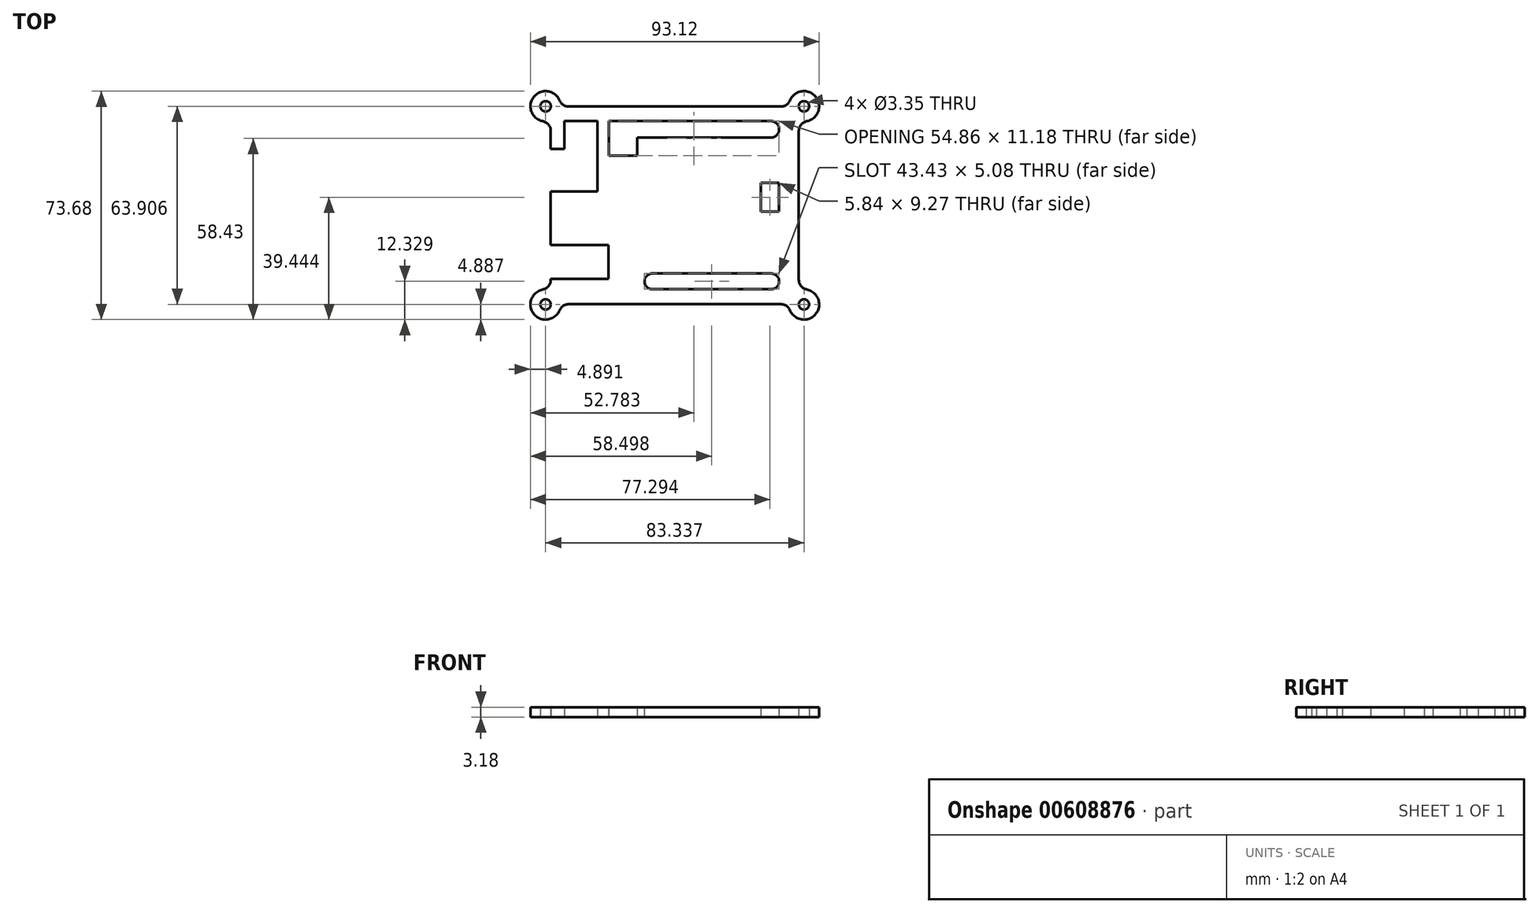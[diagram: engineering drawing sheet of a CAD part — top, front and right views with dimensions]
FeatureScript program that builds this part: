
annotation { "Feature Type Name" : "Feature", "Feature Type Description" : "" }
export const myFeature = defineFeature(function(context is Context, id is Id, definition is map)
    precondition{}
    {
        {
            var Q0;
            Q0=qCreatedBy(makeId("Top.planeOp"),FACE);
            var sketch = newSketch(context, id + "F0", { "sketchPlane" : qUnion([Q0])});
            skPoint(sketch, "E0.middle", {"position": v(0, 0) * mm});
            skLineSegment(sketch, "E1.bottom", {"start": v(-34.22, 31.88) * mm, "end": v(34.22, 31.88) * mm});
            skLineSegment(sketch, "E1.top", {"start": v(-34.22, -31.88) * mm, "end": v(34.22, -31.88) * mm});
            skLineSegment(sketch, "E1.left", {"start": v(-40, 24.03) * mm, "end": v(-40, 18.16) * mm});
            skLineSegment(sketch, "E1.right", {"start": v(40, 24.03) * mm, "end": v(40, -24.03) * mm});
            skArc(sketch, "E2", {"start": v(-37.15, 33.83) * mm, "mid": v(-45.46, 35.04) * mm, "end": v(-42.58, 27.15) * mm});
            skArc(sketch, "E3.filletArc", {"start": v(-37.15, 33.83) * mm, "mid": v(-35.98, 32.41) * mm, "end": v(-34.22, 31.88) * mm});
            skArc(sketch, "E4.filletArc", {"start": v(-40, 24.03) * mm, "mid": v(-40.73, 26.06) * mm, "end": v(-42.58, 27.15) * mm});
            skArc(sketch, "E5", {"start": v(-42.59, -27.15) * mm, "mid": v(-45.46, -35.04) * mm, "end": v(-37.15, -33.83) * mm});
            skArc(sketch, "E6.filletArc", {"start": v(-42.59, -27.15) * mm, "mid": v(-40.73, -26.06) * mm, "end": v(-40, -24.03) * mm});
            skArc(sketch, "E7.filletArc", {"start": v(-34.22, -31.88) * mm, "mid": v(-35.99, -32.41) * mm, "end": v(-37.15, -33.83) * mm});
            skArc(sketch, "E8", {"start": v(37.15, -33.83) * mm, "mid": v(45.46, -35.04) * mm, "end": v(42.59, -27.15) * mm});
            skArc(sketch, "E9.filletArc", {"start": v(40, -24.03) * mm, "mid": v(40.73, -26.06) * mm, "end": v(42.59, -27.15) * mm});
            skArc(sketch, "E10.filletArc", {"start": v(37.15, -33.83) * mm, "mid": v(35.99, -32.41) * mm, "end": v(34.22, -31.88) * mm});
            skArc(sketch, "E11", {"start": v(42.59, 27.15) * mm, "mid": v(45.46, 35.04) * mm, "end": v(37.15, 33.83) * mm});
            skArc(sketch, "E12.filletArc", {"start": v(34.22, 31.88) * mm, "mid": v(35.99, 32.41) * mm, "end": v(37.15, 33.83) * mm});
            skArc(sketch, "E13.filletArc", {"start": v(42.59, 27.15) * mm, "mid": v(40.73, 26.06) * mm, "end": v(40, 24.03) * mm});
            skCircle(sketch, "E14", {"center": v(-41.66, 31.95) * mm, "radius": 1.68 * mm});
            skCircle(sketch, "E15", {"center": v(-41.67, -31.95) * mm, "radius": 1.68 * mm});
            skCircle(sketch, "E16", {"center": v(41.67, -31.95) * mm, "radius": 1.68 * mm});
            skCircle(sketch, "E17", {"center": v(41.67, 31.95) * mm, "radius": 1.68 * mm});
            skLineSegment(sketch, "E18.0", {"start": v(-35.56, 27.18) * mm, "end": v(-24.9, 27.18) * mm});
            skLineSegment(sketch, "E19.0", {"start": v(-35.56, 27.18) * mm, "end": v(-35.56, 18.16) * mm});
            skLineSegment(sketch, "E20.0", {"start": v(-24.9, 27.18) * mm, "end": v(-24.9, 4.45) * mm});
            skLineSegment(sketch, "E21.0", {"start": v(-35.56, 4.45) * mm, "end": v(-24.9, 4.45) * mm});
            skLineSegment(sketch, "E22", {"start": v(-35.56, 18.16) * mm, "end": v(-40, 18.16) * mm});
            skLineSegment(sketch, "E23", {"start": v(-35.56, 4.45) * mm, "end": v(-40, 4.45) * mm});
            skLineSegment(sketch, "E24.trimOffspring", {"start": v(-40, 4.45) * mm, "end": v(-40, -12.83) * mm});
            skLineSegment(sketch, "E25.0", {"start": v(-40, -12.83) * mm, "end": v(-21.34, -12.83) * mm});
            skLineSegment(sketch, "E26.0", {"start": v(-40, -23.75) * mm, "end": v(-21.34, -23.75) * mm});
            skLineSegment(sketch, "E27.0", {"start": v(-21.34, -12.83) * mm, "end": v(-21.34, -23.75) * mm});
            skLineSegment(sketch, "E28.trimOffspring", {"start": v(-40, -23.75) * mm, "end": v(-40, -24.03) * mm});
            skLineSegment(sketch, "E29.0", {"start": v(-21.2, 27.18) * mm, "end": v(-21.2, 16) * mm});
            skLineSegment(sketch, "E30.trimOffspring", {"start": v(-12.07, 21.84) * mm, "end": v(30.99, 21.84) * mm});
            skLineSegment(sketch, "E31.trimOffspring", {"start": v(-21.2, 27.18) * mm, "end": v(30.99, 27.18) * mm});
            skLineSegment(sketch, "E32.0", {"start": v(-21.2, 16) * mm, "end": v(-12.07, 16) * mm});
            skLineSegment(sketch, "E33", {"start": v(-12.07, 21.84) * mm, "end": v(-12.07, 16) * mm});
            skLineSegment(sketch, "E34.0", {"start": v(33.65, 24.51) * mm, "end": v(33.65, 24.51) * mm});
            skArc(sketch, "E35.filletArc", {"start": v(33.65, 24.51) * mm, "mid": v(32.87, 26.4) * mm, "end": v(30.99, 27.18) * mm});
            skArc(sketch, "E36.filletArc", {"start": v(30.99, 21.84) * mm, "mid": v(32.87, 22.63) * mm, "end": v(33.65, 24.51) * mm});
            skLineSegment(sketch, "E37.0", {"start": v(-7.24, -27.05) * mm, "end": v(31.12, -27.05) * mm});
            skLineSegment(sketch, "E38.0", {"start": v(33.66, -24.51) * mm, "end": v(33.66, -24.51) * mm});
            skLineSegment(sketch, "E39.0", {"start": v(-9.78, 24.03) * mm, "end": v(-9.78, 21.84) * mm});
            skLineSegment(sketch, "E40.trimOffspring", {"start": v(-9.78, -24.51) * mm, "end": v(-9.78, -24.51) * mm});
            skLineSegment(sketch, "E41.trimOffspring", {"start": v(-7.24, -21.97) * mm, "end": v(31.12, -21.97) * mm});
            skArc(sketch, "E42.filletArc", {"start": v(-7.24, -21.97) * mm, "mid": v(-9.04, -22.71) * mm, "end": v(-9.78, -24.51) * mm});
            skArc(sketch, "E43.filletArc", {"start": v(-9.78, -24.51) * mm, "mid": v(-9.04, -26.3) * mm, "end": v(-7.24, -27.05) * mm});
            skArc(sketch, "E44.filletArc", {"start": v(31.12, -27.05) * mm, "mid": v(32.91, -26.3) * mm, "end": v(33.66, -24.51) * mm});
            skArc(sketch, "E45.filletArc", {"start": v(33.66, -24.51) * mm, "mid": v(32.91, -22.71) * mm, "end": v(31.12, -21.97) * mm});
            skLineSegment(sketch, "E46.0", {"start": v(27.81, -2.03) * mm, "end": v(33.66, -2.03) * mm});
            skLineSegment(sketch, "E47.0", {"start": v(33.66, 7.24) * mm, "end": v(33.66, -2.03) * mm});
            skLineSegment(sketch, "E48.trimOffspring", {"start": v(27.81, 7.24) * mm, "end": v(33.66, 7.24) * mm});
            skLineSegment(sketch, "E49.trimOffspring", {"start": v(27.81, 7.24) * mm, "end": v(27.81, -2.03) * mm});
            skSolve(sketch);
        }
        {
            var Q0;
            Q0 = qSketchRegion(id + "F0", true);
            extrude(context, id + "F1", {"entities" : qUnion([Q0]), "depth" : 3.17 * mm, "offsetDistance" : 25.4 * mm});
        }
    });
